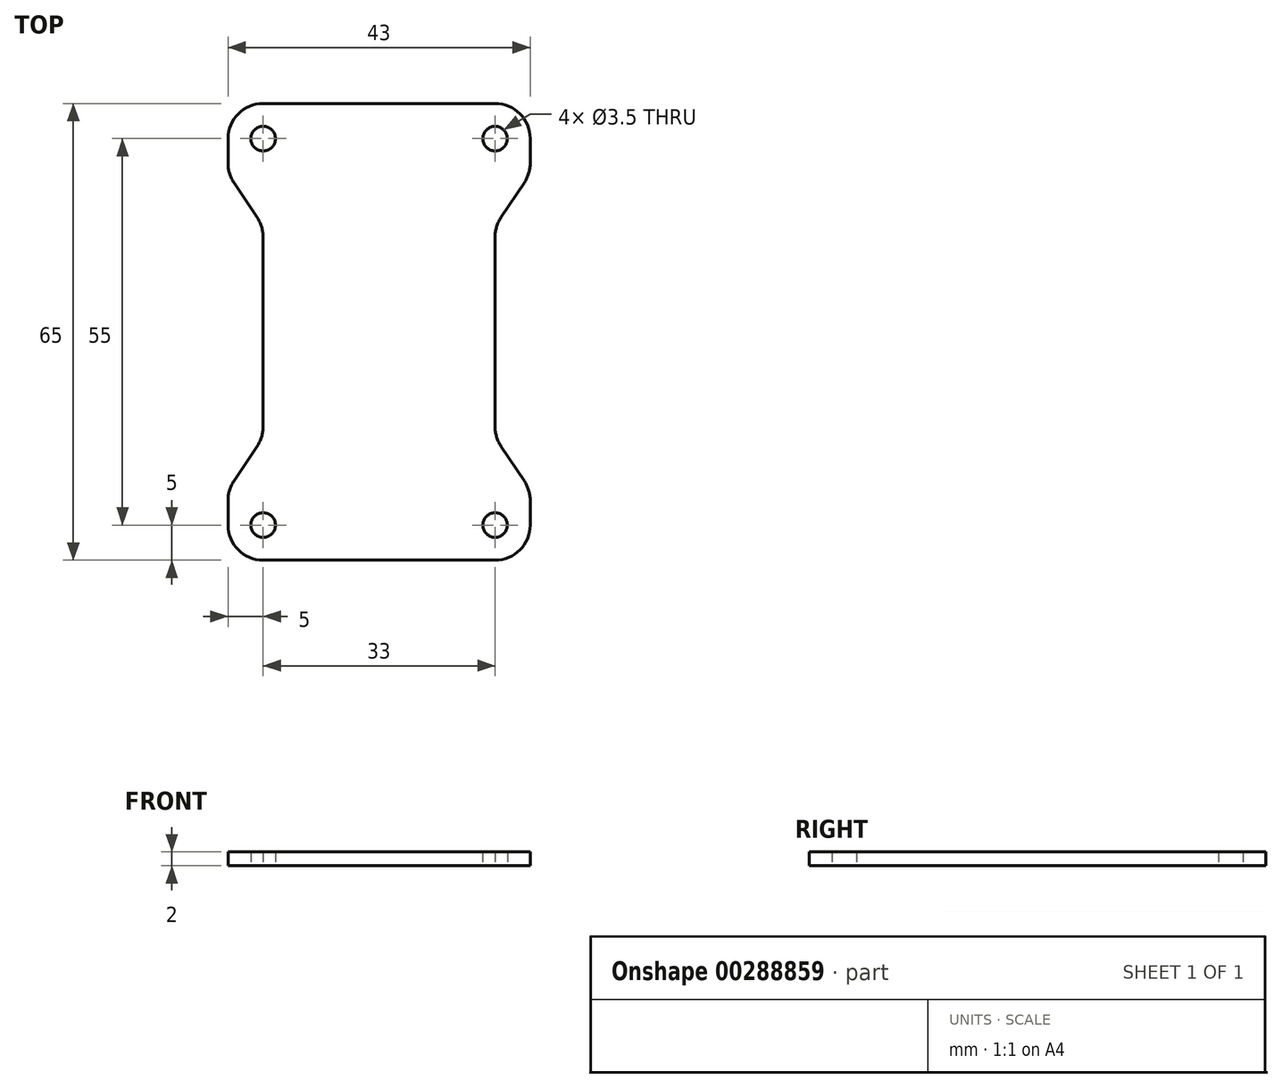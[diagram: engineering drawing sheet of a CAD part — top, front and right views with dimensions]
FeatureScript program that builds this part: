
annotation { "Feature Type Name" : "Feature", "Feature Type Description" : "" }
export const myFeature = defineFeature(function(context is Context, id is Id, definition is map)
    precondition{}
    {
        {
            var Q0;
            Q0=qCreatedBy(makeId("Top.planeOp"),FACE);
            var sketch = newSketch(context, id + "F0", { "sketchPlane" : qUnion([Q0])});
            skLineSegment(sketch, "E0", {"start": v(-21.5, 32.5) * mm, "end": v(21.5, 32.5) * mm});
            skLineSegment(sketch, "E1", {"start": v(21.5, 32.5) * mm, "end": v(21.5, 22.5) * mm});
            skLineSegment(sketch, "E2", {"start": v(21.5, 22.5) * mm, "end": v(16.5, 15) * mm});
            skLineSegment(sketch, "E3", {"start": v(16.5, 15) * mm, "end": v(16.5, -15) * mm});
            skLineSegment(sketch, "E4", {"start": v(16.5, -15) * mm, "end": v(21.5, -22.5) * mm});
            skLineSegment(sketch, "E5", {"start": v(21.5, -22.5) * mm, "end": v(21.5, -32.5) * mm});
            skLineSegment(sketch, "E6", {"start": v(21.5, -32.5) * mm, "end": v(-21.5, -32.5) * mm});
            skLineSegment(sketch, "E7", {"start": v(-21.5, -32.5) * mm, "end": v(-21.5, -22.5) * mm});
            skLineSegment(sketch, "E8", {"start": v(-21.5, -22.5) * mm, "end": v(-16.5, -15) * mm});
            skLineSegment(sketch, "E9", {"start": v(-16.5, -15) * mm, "end": v(-16.5, 15) * mm});
            skLineSegment(sketch, "E10", {"start": v(-16.5, 15) * mm, "end": v(-21.5, 22.5) * mm});
            skLineSegment(sketch, "E11", {"start": v(-21.5, 22.5) * mm, "end": v(-21.5, 32.5) * mm});
            skPoint(sketch, "E12", {"position": v(0, 32.5) * mm});
            skPoint(sketch, "E13", {"position": v(0, -32.5) * mm});
            skPoint(sketch, "E14", {"position": v(16.5, 0) * mm});
            skPoint(sketch, "E15", {"position": v(-16.5, 0) * mm});
            skSolve(sketch);
        }
        {
            var Q0;
            Q0 = qSketchRegion(id + "F0", true);
            extrude(context, id + "F1", {"entities" : qUnion([Q0]), "depth" : 2 * mm});
        }
        {
            var Q0;
            Q0=qCreatedBy(makeId("Top.planeOp"),FACE);
            var sketch = newSketch(context, id + "F2", { "sketchPlane" : qUnion([Q0])});
            skCircle(sketch, "E16", {"center": v(-16.5, 27.5) * mm, "radius": 1.75 * mm});
            skCircle(sketch, "E17", {"center": v(16.5, 27.5) * mm, "radius": 1.75 * mm});
            skCircle(sketch, "E18", {"center": v(16.5, -27.5) * mm, "radius": 1.75 * mm});
            skCircle(sketch, "E19", {"center": v(-16.5, -27.5) * mm, "radius": 1.75 * mm});
            skSolve(sketch);
        }
        {
            var Q0;
            Q0 = qSketchRegion(id + "F2", true);
            extrude(context, id + "F3", {"entities" : qUnion([Q0]), "operationType" : NewBodyOperationType.REMOVE, "depth" : 25 * mm});
        }
        {
            var Q0;
            Q0=makeQuery(id+"F1.opExtrude","SWEPT_EDGE",EDGE,{"disambiguationData":[OSD([sQuery(id+"F0.wireOp",EDGE,"E0"),sQuery(id+"F0.wireOp",EDGE,"E11")])]});
            var Q1;
            Q1=makeQuery(id+"F1.opExtrude","SWEPT_EDGE",EDGE,{"disambiguationData":[OSD([sQuery(id+"F0.wireOp",EDGE,"E0"),sQuery(id+"F0.wireOp",EDGE,"E1")])]});
            var Q2;
            Q2=makeQuery(id+"F1.opExtrude","SWEPT_EDGE",EDGE,{"disambiguationData":[OSD([sQuery(id+"F0.wireOp",EDGE,"E5"),sQuery(id+"F0.wireOp",EDGE,"E6")])]});
            var Q3;
            Q3=makeQuery(id+"F1.opExtrude","SWEPT_EDGE",EDGE,{"disambiguationData":[OSD([sQuery(id+"F0.wireOp",EDGE,"E6"),sQuery(id+"F0.wireOp",EDGE,"E7")])]});
            var Q4;
            Q4=makeQuery(id+"F1.opExtrude","SWEPT_EDGE",EDGE,{"disambiguationData":[OSD([sQuery(id+"F0.wireOp",EDGE,"E1"),sQuery(id+"F0.wireOp",EDGE,"E2")])]});
            var Q5;
            Q5=makeQuery(id+"F1.opExtrude","SWEPT_EDGE",EDGE,{"disambiguationData":[OSD([sQuery(id+"F0.wireOp",EDGE,"E2"),sQuery(id+"F0.wireOp",EDGE,"E3")])]});
            var Q6;
            Q6=makeQuery(id+"F1.opExtrude","SWEPT_EDGE",EDGE,{"disambiguationData":[OSD([sQuery(id+"F0.wireOp",EDGE,"E3"),sQuery(id+"F0.wireOp",EDGE,"E4")])]});
            var Q7;
            Q7=makeQuery(id+"F1.opExtrude","SWEPT_EDGE",EDGE,{"disambiguationData":[OSD([sQuery(id+"F0.wireOp",EDGE,"E4"),sQuery(id+"F0.wireOp",EDGE,"E5")])]});
            var Q8;
            Q8=makeQuery(id+"F1.opExtrude","SWEPT_EDGE",EDGE,{"disambiguationData":[OSD([sQuery(id+"F0.wireOp",EDGE,"E7"),sQuery(id+"F0.wireOp",EDGE,"E8")])]});
            var Q9;
            Q9=makeQuery(id+"F1.opExtrude","SWEPT_EDGE",EDGE,{"disambiguationData":[OSD([sQuery(id+"F0.wireOp",EDGE,"E8"),sQuery(id+"F0.wireOp",EDGE,"E9")])]});
            var Q10;
            Q10=makeQuery(id+"F1.opExtrude","SWEPT_EDGE",EDGE,{"disambiguationData":[OSD([sQuery(id+"F0.wireOp",EDGE,"E9"),sQuery(id+"F0.wireOp",EDGE,"E10")])]});
            var Q11;
            Q11=makeQuery(id+"F1.opExtrude","SWEPT_EDGE",EDGE,{"disambiguationData":[OSD([sQuery(id+"F0.wireOp",EDGE,"E10"),sQuery(id+"F0.wireOp",EDGE,"E11")])]});
            fillet(context, id + "F4", {"entities" : qUnion([Q0, Q1, Q2, Q3, Q4, Q5, Q6, Q7, Q8, Q9, Q10, Q11]), "radius" : 5 * mm, "tangentPropagation" : true, "allowEdgeOverflow" : false});
        }
    });
